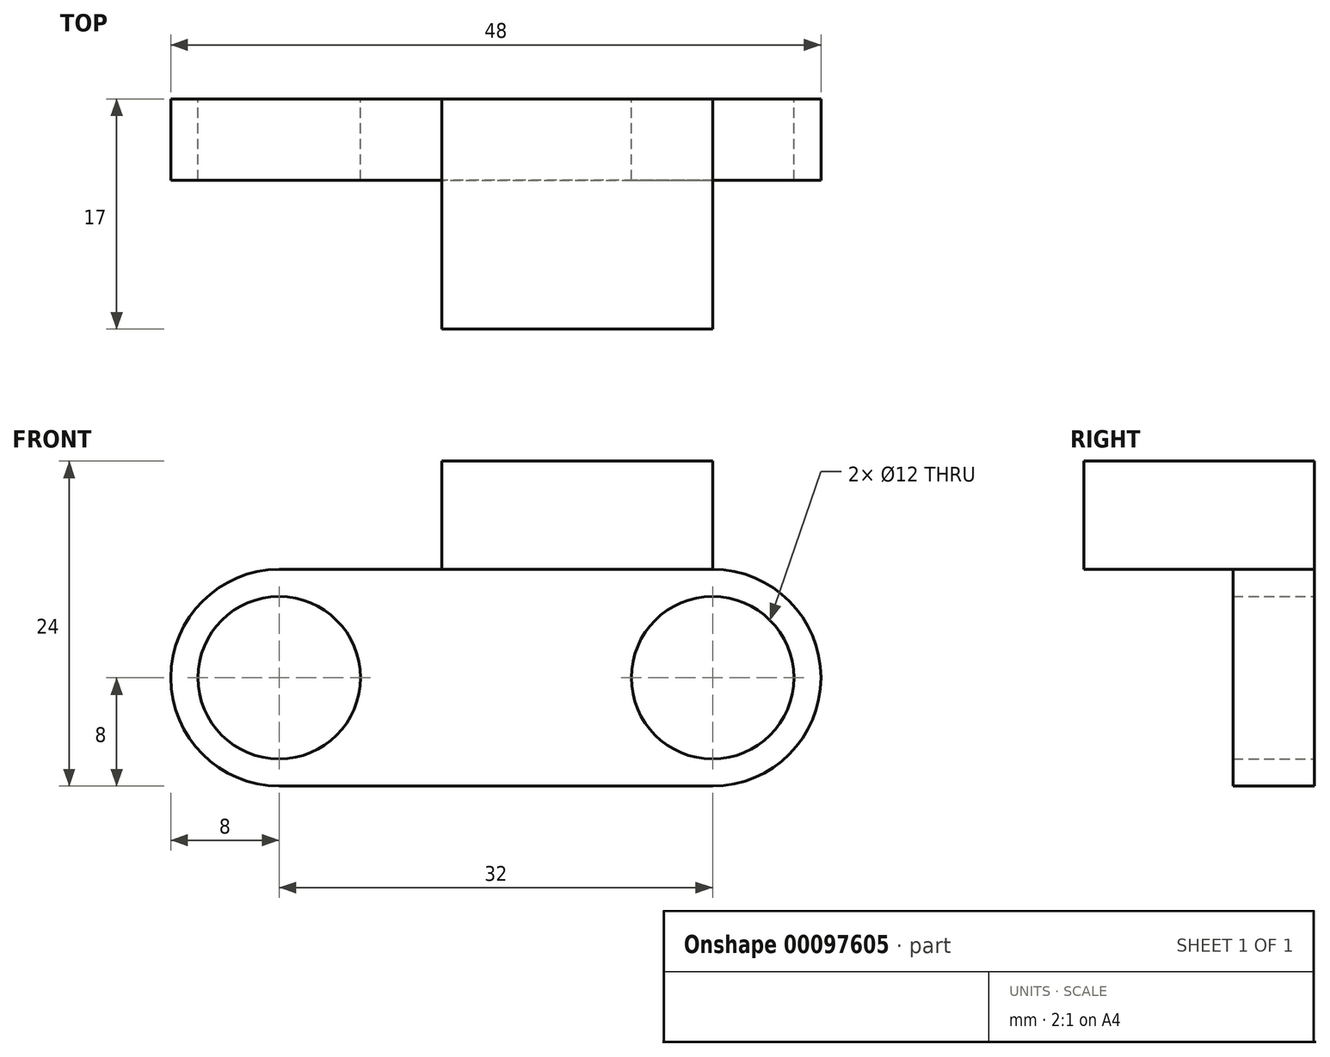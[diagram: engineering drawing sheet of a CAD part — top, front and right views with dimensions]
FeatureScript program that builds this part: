
annotation { "Feature Type Name" : "Feature", "Feature Type Description" : "" }
export const myFeature = defineFeature(function(context is Context, id is Id, definition is map)
    precondition{}
    {
        {
            var Q0;
            Q0=qCreatedBy(makeId("Front.planeOp"),FACE);
            var sketch = newSketch(context, id + "F0", { "sketchPlane" : qUnion([Q0])});
            skLineSegment(sketch, "E0", {"start": v(-12, -16) * mm, "end": v(20, -16) * mm});
            skArc(sketch, "E1", {"start": v(20, -16) * mm, "mid": v(28, -8) * mm, "end": v(20, 0) * mm});
            skArc(sketch, "E2", {"start": v(-12, -16) * mm, "mid": v(-20, -8) * mm, "end": v(-12, 0) * mm});
            skLineSegment(sketch, "E3", {"start": v(20, 0) * mm, "end": v(20, 0) * mm});
            skLineSegment(sketch, "E4", {"start": v(20, 0) * mm, "end": v(20, 8) * mm});
            skLineSegment(sketch, "E5", {"start": v(20, 8) * mm, "end": v(0, 8) * mm});
            skLineSegment(sketch, "E6", {"start": v(0, 8) * mm, "end": v(0, 0) * mm});
            skLineSegment(sketch, "E7", {"start": v(0, 0) * mm, "end": v(-12, 0) * mm});
            skCircle(sketch, "E8", {"center": v(-12, -8) * mm, "radius": 6 * mm});
            skCircle(sketch, "E9", {"center": v(20, -8) * mm, "radius": 6 * mm});
            skSolve(sketch);
        }
        {
            var Q0;
            Q0=qCreatedBy(makeId("Front.planeOp"),FACE);
            var sketch = newSketch(context, id + "F1", { "sketchPlane" : qUnion([Q0])});
            skLineSegment(sketch, "E10", {"start": v(0, 0) * mm, "end": v(0, 8) * mm});
            skLineSegment(sketch, "E11", {"start": v(0, 8) * mm, "end": v(20, 8) * mm});
            skLineSegment(sketch, "E12", {"start": v(20, 8) * mm, "end": v(20, 0) * mm});
            skLineSegment(sketch, "E13", {"start": v(0, 0) * mm, "end": v(-12, 0) * mm});
            skLineSegment(sketch, "E14", {"start": v(-12, -16) * mm, "end": v(20, -16) * mm});
            skArc(sketch, "E15", {"start": v(20, -16) * mm, "mid": v(28, -8) * mm, "end": v(20, 0) * mm});
            skArc(sketch, "E16", {"start": v(-12, 0) * mm, "mid": v(-20, -8) * mm, "end": v(-12, -16) * mm});
            skCircle(sketch, "E17", {"center": v(-12, -8) * mm, "radius": 6 * mm});
            skCircle(sketch, "E18", {"center": v(20, -8) * mm, "radius": 6 * mm});
            skSolve(sketch);
        }
        {
            var Q0;
            Q0 = qSketchRegion(id + "F0", true);
            extrude(context, id + "F2", {"entities" : qUnion([Q0]), "depth" : 3 * mm});
        }
        {
            var Q0;
            Q0=qCreatedBy(makeId("Front.planeOp"),FACE);
            var sketch = newSketch(context, id + "F3", { "sketchPlane" : qUnion([Q0])});
            skLineSegment(sketch, "E19", {"start": v(0, 0) * mm, "end": v(20, 0) * mm});
            skLineSegment(sketch, "E20", {"start": v(20, 0) * mm, "end": v(20, 8) * mm});
            skLineSegment(sketch, "E21", {"start": v(20, 8) * mm, "end": v(0, 8) * mm});
            skLineSegment(sketch, "E22", {"start": v(0, 8) * mm, "end": v(0, 0) * mm});
            skSolve(sketch);
        }
        {
            var Q0;
            Q0 = qSketchRegion(id + "F3", true);
            extrude(context, id + "F4", {"entities" : qUnion([Q0]), "operationType" : NewBodyOperationType.ADD, "depth" : 14 * mm});
        }
        {
            var Q0;
            Q0 = qSketchRegion(id + "F1", true);
            var Q1;
            Q1=makeQuery(id+"F4.opExtrude","CAP_FACE",FACE,{"disambiguationData":[OSD([sQuery(id+"F3.wireOp",EDGE,"E19"),sQuery(id+"F3.wireOp",EDGE,"E20"),sQuery(id+"F3.wireOp",EDGE,"E21"),sQuery(id+"F3.wireOp",EDGE,"E22")])],"isStart":false});
            extrude(context, id + "F5", {"entities" : qUnion([Q0, Q1]), "operationType" : NewBodyOperationType.ADD, "oppositeDirection" : true, "depth" : 3 * mm});
        }
    });
